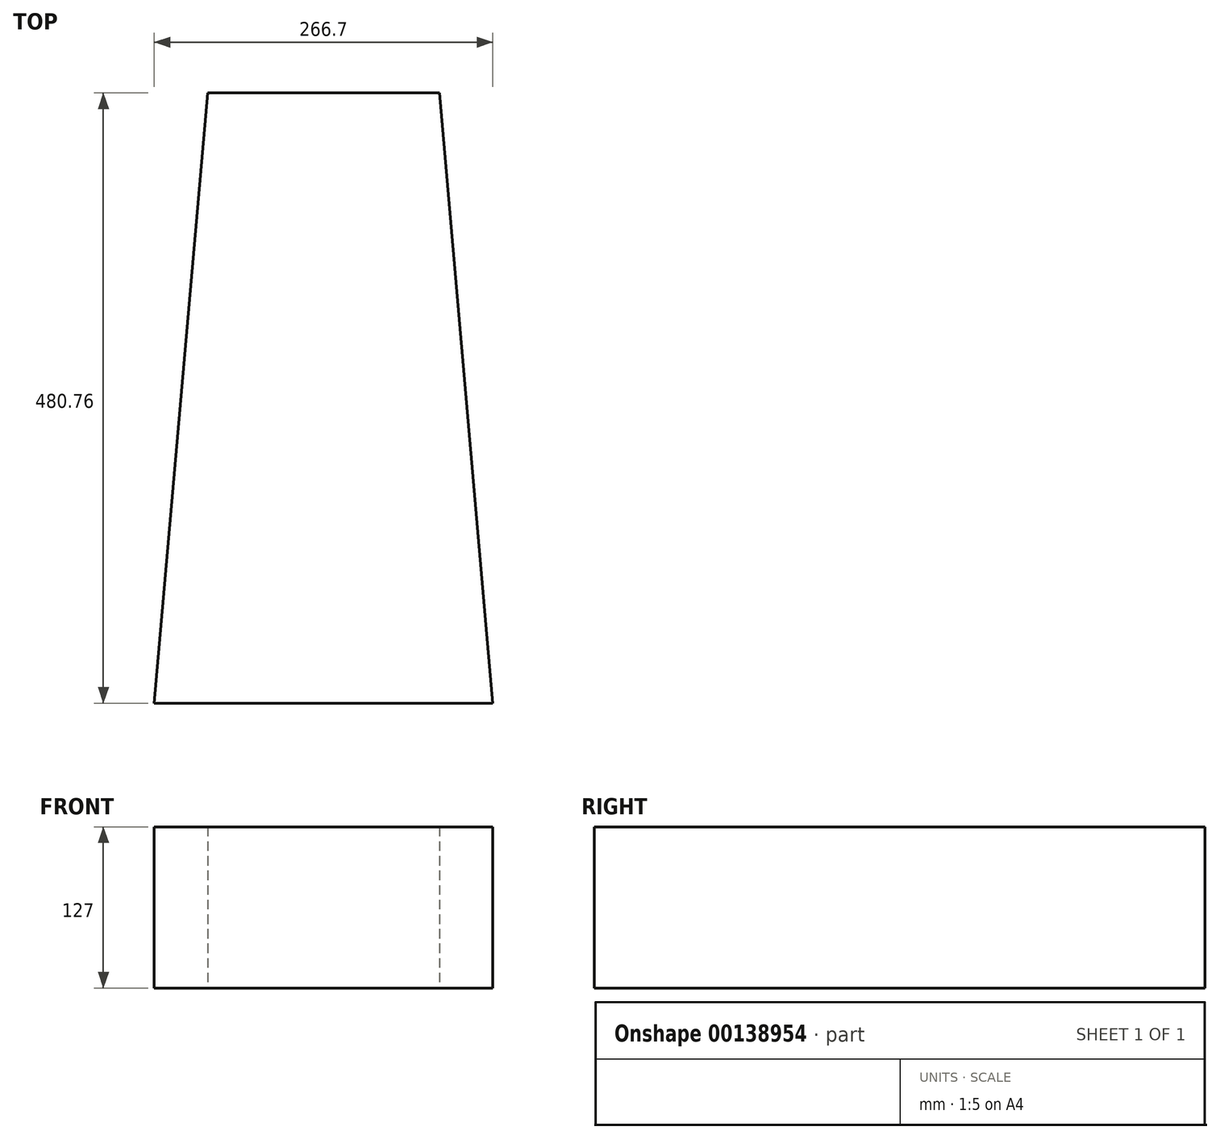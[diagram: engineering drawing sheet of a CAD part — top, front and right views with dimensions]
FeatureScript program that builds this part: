
annotation { "Feature Type Name" : "Feature", "Feature Type Description" : "" }
export const myFeature = defineFeature(function(context is Context, id is Id, definition is map)
    precondition{}
    {
        {
            var Q0;
            Q0=qCreatedBy(makeId("Top.planeOp"),FACE);
            var sketch = newSketch(context, id + "F0", { "sketchPlane" : qUnion([Q0])});
            skLineSegment(sketch, "E0", {"start": v(0, 0) * mm, "end": v(266.7, 0) * mm});
            skLineSegment(sketch, "E1", {"start": v(266.7, 0) * mm, "end": v(224.64, 480.76) * mm});
            skLineSegment(sketch, "E2", {"start": v(0, 0) * mm, "end": v(42.06, 480.76) * mm});
            skLineSegment(sketch, "E3", {"start": v(42.06, 480.76) * mm, "end": v(224.64, 480.76) * mm});
            skSolve(sketch);
        }
        {
            var Q0;
            Q0 = qSketchRegion(id + "F0", true);
            extrude(context, id + "F1", {"entities" : qUnion([Q0]), "depth" : 127 * mm});
        }
    });
